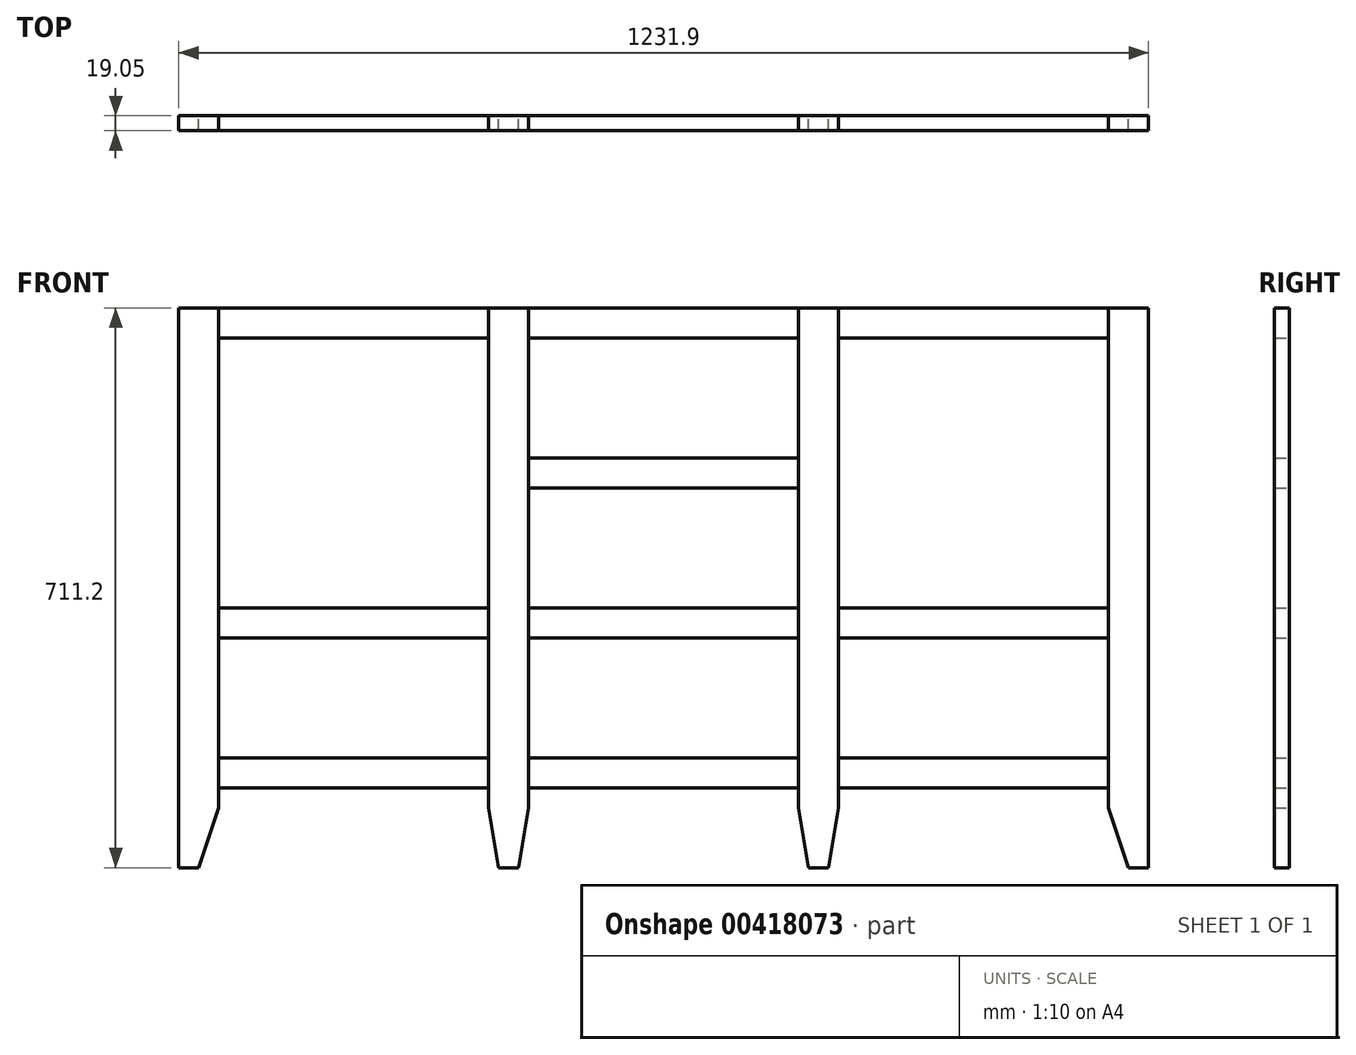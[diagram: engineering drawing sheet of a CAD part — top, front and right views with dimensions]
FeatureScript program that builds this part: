
annotation { "Feature Type Name" : "Feature", "Feature Type Description" : "" }
export const myFeature = defineFeature(function(context is Context, id is Id, definition is map)
    precondition{}
    {
        {
            var Q0;
            Q0=qCreatedBy(makeId("Front.planeOp"),FACE);
            var sketch = newSketch(context, id + "F0", { "sketchPlane" : qUnion([Q0])});
            skLineSegment(sketch, "E0.bottom", {"start": v(-222.25, 332.05) * mm, "end": v(-171.45, 332.05) * mm});
            skLineSegment(sketch, "E0.left", {"start": v(-222.25, 332.05) * mm, "end": v(-222.25, -302.95) * mm});
            skLineSegment(sketch, "E0.right", {"start": v(-171.45, 332.05) * mm, "end": v(-171.45, -302.95) * mm});
            skLineSegment(sketch, "E1.MirrorCS", {"start": v(171.45, 332.05) * mm, "end": v(171.45, -302.95) * mm});
            skLineSegment(sketch, "E2.MirrorCS", {"start": v(222.25, 332.05) * mm, "end": v(222.25, -302.95) * mm});
            skLineSegment(sketch, "E3.MirrorCS", {"start": v(196.85, -379.15) * mm, "end": v(184.15, -379.15) * mm});
            skLineSegment(sketch, "E4.MirrorCS", {"start": v(222.25, 332.05) * mm, "end": v(171.45, 332.05) * mm});
            skLineSegment(sketch, "E5.MirrorCS", {"start": v(-171.45, 332.05) * mm, "end": v(-171.45, -277.55) * mm});
            skLineSegment(sketch, "E6.bottom", {"start": v(-171.45, 332.05) * mm, "end": v(171.45, 332.05) * mm});
            skLineSegment(sketch, "E6.top", {"start": v(-171.45, 293.95) * mm, "end": v(171.45, 293.95) * mm});
            skLineSegment(sketch, "E6.left", {"start": v(-171.45, 332.05) * mm, "end": v(-171.45, 293.95) * mm});
            skLineSegment(sketch, "E6.right", {"start": v(171.45, 332.05) * mm, "end": v(171.45, 293.95) * mm});
            skLineSegment(sketch, "E7.bottom", {"start": v(-171.45, 141.55) * mm, "end": v(171.45, 141.55) * mm});
            skLineSegment(sketch, "E7.top", {"start": v(-171.45, 103.45) * mm, "end": v(171.45, 103.45) * mm});
            skLineSegment(sketch, "E7.left", {"start": v(-171.45, 141.55) * mm, "end": v(-171.45, 103.45) * mm});
            skLineSegment(sketch, "E7.right", {"start": v(171.45, 141.55) * mm, "end": v(171.45, 103.45) * mm});
            skLineSegment(sketch, "E8.bottom", {"start": v(-171.45, -48.95) * mm, "end": v(171.45, -48.95) * mm});
            skLineSegment(sketch, "E8.top", {"start": v(-171.45, -87.05) * mm, "end": v(171.45, -87.05) * mm});
            skLineSegment(sketch, "E8.left", {"start": v(-171.45, -48.95) * mm, "end": v(-171.45, -87.05) * mm});
            skLineSegment(sketch, "E8.right", {"start": v(171.45, -48.95) * mm, "end": v(171.45, -87.05) * mm});
            skLineSegment(sketch, "E9.bottom", {"start": v(-171.45, -239.45) * mm, "end": v(171.45, -239.45) * mm});
            skLineSegment(sketch, "E9.top", {"start": v(-171.45, -277.55) * mm, "end": v(171.45, -277.55) * mm});
            skLineSegment(sketch, "E9.left", {"start": v(-171.45, -239.45) * mm, "end": v(-171.45, -277.55) * mm});
            skLineSegment(sketch, "E9.right", {"start": v(171.45, -239.45) * mm, "end": v(171.45, -277.55) * mm});
            skLineSegment(sketch, "E10.top", {"start": v(-565.15, 332.05) * mm, "end": v(-615.95, 332.05) * mm});
            skLineSegment(sketch, "E10.left", {"start": v(-565.15, 332.05) * mm, "end": v(-565.15, 332.05) * mm});
            skLineSegment(sketch, "E11.left", {"start": v(-615.95, 332.05) * mm, "end": v(-615.95, -379.15) * mm});
            skLineSegment(sketch, "E11.right", {"start": v(-565.15, 332.05) * mm, "end": v(-565.15, -302.95) * mm});
            skLineSegment(sketch, "E12.bottom", {"start": v(565.15, 332.05) * mm, "end": v(615.95, 332.05) * mm});
            skLineSegment(sketch, "E12.top", {"start": v(590.55, -379.15) * mm, "end": v(615.95, -379.15) * mm});
            skLineSegment(sketch, "E12.left", {"start": v(565.15, 332.05) * mm, "end": v(565.15, -302.95) * mm});
            skLineSegment(sketch, "E12.right", {"start": v(615.95, 332.05) * mm, "end": v(615.95, -379.15) * mm});
            skLineSegment(sketch, "E13.bottom", {"start": v(-565.15, 332.05) * mm, "end": v(-222.25, 332.05) * mm});
            skLineSegment(sketch, "E13.top", {"start": v(-565.15, 293.95) * mm, "end": v(-222.25, 293.95) * mm});
            skLineSegment(sketch, "E13.left", {"start": v(-565.15, 332.05) * mm, "end": v(-565.15, 293.95) * mm});
            skLineSegment(sketch, "E13.right", {"start": v(-222.25, 332.05) * mm, "end": v(-222.25, 293.95) * mm});
            skLineSegment(sketch, "E14.bottom", {"start": v(222.25, 332.05) * mm, "end": v(565.15, 332.05) * mm});
            skLineSegment(sketch, "E14.top", {"start": v(222.25, 293.95) * mm, "end": v(565.15, 293.95) * mm});
            skLineSegment(sketch, "E14.left", {"start": v(222.25, 332.05) * mm, "end": v(222.25, 293.95) * mm});
            skLineSegment(sketch, "E14.right", {"start": v(565.15, 332.05) * mm, "end": v(565.15, 293.95) * mm});
            skLineSegment(sketch, "E15.bottom", {"start": v(-222.25, -48.95) * mm, "end": v(-565.15, -48.95) * mm});
            skLineSegment(sketch, "E15.top", {"start": v(-222.25, -87.05) * mm, "end": v(-565.15, -87.05) * mm});
            skLineSegment(sketch, "E15.left", {"start": v(-222.25, -48.95) * mm, "end": v(-222.25, -87.05) * mm});
            skLineSegment(sketch, "E15.right", {"start": v(-565.15, -48.95) * mm, "end": v(-565.15, -87.05) * mm});
            skLineSegment(sketch, "E16.bottom", {"start": v(222.25, -48.95) * mm, "end": v(565.15, -48.95) * mm});
            skLineSegment(sketch, "E16.top", {"start": v(222.25, -87.05) * mm, "end": v(565.15, -87.05) * mm});
            skLineSegment(sketch, "E16.left", {"start": v(222.25, -48.95) * mm, "end": v(222.25, -87.05) * mm});
            skLineSegment(sketch, "E16.right", {"start": v(565.15, -48.95) * mm, "end": v(565.15, -87.05) * mm});
            skLineSegment(sketch, "E17.bottom", {"start": v(-222.25, -239.45) * mm, "end": v(-565.15, -239.45) * mm});
            skLineSegment(sketch, "E17.top", {"start": v(-222.25, -277.55) * mm, "end": v(-565.15, -277.55) * mm});
            skLineSegment(sketch, "E17.left", {"start": v(-222.25, -239.45) * mm, "end": v(-222.25, -277.55) * mm});
            skLineSegment(sketch, "E17.right", {"start": v(-565.15, -239.45) * mm, "end": v(-565.15, -277.55) * mm});
            skPoint(sketch, "E18.oppositeSnap0", {"position": v(0, -277.55) * mm});
            skLineSegment(sketch, "E18.bottom", {"start": v(222.25, -239.45) * mm, "end": v(565.15, -239.45) * mm});
            skLineSegment(sketch, "E18.top", {"start": v(222.25, -277.55) * mm, "end": v(565.15, -277.55) * mm});
            skLineSegment(sketch, "E18.left", {"start": v(222.25, -239.45) * mm, "end": v(222.25, -277.55) * mm});
            skLineSegment(sketch, "E18.right", {"start": v(565.15, -239.45) * mm, "end": v(565.15, -277.55) * mm});
            skLineSegment(sketch, "E19", {"start": v(590.55, -379.15) * mm, "end": v(565.15, -302.95) * mm});
            skPoint(sketch, "E20.orphan", {"position": v(565.15, -379.15) * mm});
            skPoint(sketch, "E21.orphan", {"position": v(-222.25, -379.15) * mm});
            skPoint(sketch, "E22.orphan", {"position": v(222.25, -379.15) * mm});
            skLineSegment(sketch, "E23", {"start": v(-184.15, -379.15) * mm, "end": v(-209.55, -379.15) * mm});
            skLineSegment(sketch, "E24", {"start": v(-222.25, -302.95) * mm, "end": v(-209.55, -379.15) * mm});
            skLineSegment(sketch, "E25", {"start": v(-184.15, -379.15) * mm, "end": v(-171.45, -302.95) * mm});
            skPoint(sketch, "E26.orphan", {"position": v(-171.45, -379.15) * mm});
            skLineSegment(sketch, "E27", {"start": v(196.85, -379.15) * mm, "end": v(209.55, -379.15) * mm});
            skLineSegment(sketch, "E28", {"start": v(209.55, -379.15) * mm, "end": v(222.25, -302.95) * mm});
            skLineSegment(sketch, "E29", {"start": v(184.15, -379.15) * mm, "end": v(171.45, -302.95) * mm});
            skPoint(sketch, "E30.orphan", {"position": v(171.45, -379.15) * mm});
            skLineSegment(sketch, "E31", {"start": v(-615.95, -379.15) * mm, "end": v(-590.55, -379.15) * mm});
            skLineSegment(sketch, "E32", {"start": v(-590.55, -379.15) * mm, "end": v(-565.15, -302.95) * mm});
            skSolve(sketch);
        }
        {
            var Q0;
            Q0=makeQuery(id+"F0.imprint","IMPRINT",FACE,{"disambiguationData":[TD([[makeQuery(id+"F0.imprint","IMPRINT",EDGE,{"derivedFrom":sQuery(id+"F0.wireOp",EDGE,"E10.top")}),1.0]])]});
            var Q1;
            Q1=makeQuery(id+"F0.imprint","IMPRINT",FACE,{"disambiguationData":[TD([[makeQuery(id+"F0.imprint","IMPRINT",EDGE,{"derivedFrom":sQuery(id+"F0.wireOp",EDGE,"E0.bottom")}),-1.0]])]});
            var Q2;
            Q2=makeQuery(id+"F0.imprint","IMPRINT",FACE,{"disambiguationData":[TD([[makeQuery(id+"F0.imprint","IMPRINT",EDGE,{"derivedFrom":sQuery(id+"F0.wireOp",EDGE,"E3.MirrorCS")}),-1.0]])]});
            var Q3;
            Q3=makeQuery(id+"F0.imprint","IMPRINT",FACE,{"disambiguationData":[TD([[makeQuery(id+"F0.imprint","IMPRINT",EDGE,{"derivedFrom":sQuery(id+"F0.wireOp",EDGE,"E12.bottom")}),-1.0]])]});
            extrude(context, id + "F1", {"entities" : qUnion([Q0, Q1, Q2, Q3]), "depth" : 19.05 * mm});
        }
        {
            var Q0;
            Q0=makeQuery(id+"F0.imprint","IMPRINT",FACE,{"disambiguationData":[TD([[makeQuery(id+"F0.imprint","IMPRINT",EDGE,{"derivedFrom":sQuery(id+"F0.wireOp",EDGE,"E13.bottom")}),-1.0]])]});
            var Q1;
            Q1=makeQuery(id+"F0.imprint","IMPRINT",FACE,{"disambiguationData":[TD([[makeQuery(id+"F0.imprint","IMPRINT",EDGE,{"derivedFrom":sQuery(id+"F0.wireOp",EDGE,"E15.bottom")}),1.0]])]});
            var Q2;
            Q2=makeQuery(id+"F0.imprint","IMPRINT",FACE,{"disambiguationData":[TD([[makeQuery(id+"F0.imprint","IMPRINT",EDGE,{"derivedFrom":sQuery(id+"F0.wireOp",EDGE,"E17.bottom")}),1.0]])]});
            var Q3;
            Q3=makeQuery(id+"F0.imprint","IMPRINT",FACE,{"disambiguationData":[TD([[makeQuery(id+"F0.imprint","IMPRINT",EDGE,{"derivedFrom":sQuery(id+"F0.wireOp",EDGE,"E6.bottom")}),-1.0]])]});
            var Q4;
            Q4=makeQuery(id+"F0.imprint","IMPRINT",FACE,{"disambiguationData":[TD([[makeQuery(id+"F0.imprint","IMPRINT",EDGE,{"derivedFrom":sQuery(id+"F0.wireOp",EDGE,"E7.bottom")}),-1.0]])]});
            var Q5;
            Q5=makeQuery(id+"F0.imprint","IMPRINT",FACE,{"disambiguationData":[TD([[makeQuery(id+"F0.imprint","IMPRINT",EDGE,{"derivedFrom":sQuery(id+"F0.wireOp",EDGE,"E8.bottom")}),-1.0]])]});
            var Q6;
            Q6=makeQuery(id+"F0.imprint","IMPRINT",FACE,{"disambiguationData":[TD([[makeQuery(id+"F0.imprint","IMPRINT",EDGE,{"derivedFrom":sQuery(id+"F0.wireOp",EDGE,"E9.bottom")}),-1.0]])]});
            var Q7;
            Q7=makeQuery(id+"F0.imprint","IMPRINT",FACE,{"disambiguationData":[TD([[makeQuery(id+"F0.imprint","IMPRINT",EDGE,{"derivedFrom":sQuery(id+"F0.wireOp",EDGE,"E18.bottom")}),-1.0]])]});
            var Q8;
            Q8=makeQuery(id+"F0.imprint","IMPRINT",FACE,{"disambiguationData":[TD([[makeQuery(id+"F0.imprint","IMPRINT",EDGE,{"derivedFrom":sQuery(id+"F0.wireOp",EDGE,"E16.bottom")}),-1.0]])]});
            var Q9;
            Q9=makeQuery(id+"F0.imprint","IMPRINT",FACE,{"disambiguationData":[TD([[makeQuery(id+"F0.imprint","IMPRINT",EDGE,{"derivedFrom":sQuery(id+"F0.wireOp",EDGE,"E14.bottom")}),-1.0]])]});
            extrude(context, id + "F2", {"entities" : qUnion([Q0, Q1, Q2, Q3, Q4, Q5, Q6, Q7, Q8, Q9]), "depth" : 19.05 * mm});
        }
    });
